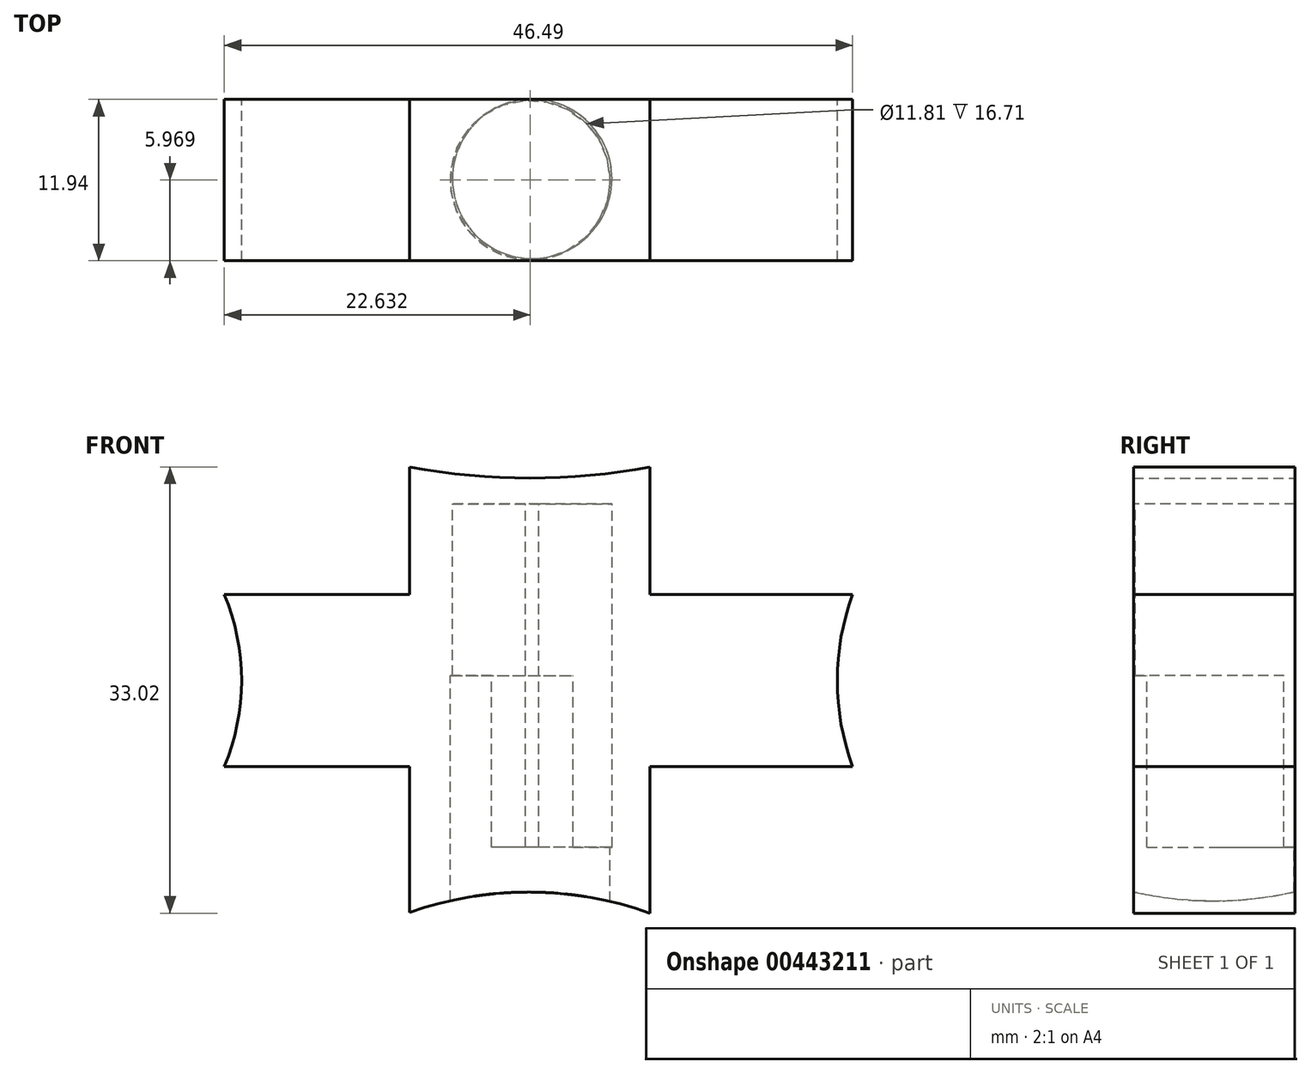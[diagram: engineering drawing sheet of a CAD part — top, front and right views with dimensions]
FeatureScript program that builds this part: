
annotation { "Feature Type Name" : "Feature", "Feature Type Description" : "" }
export const myFeature = defineFeature(function(context is Context, id is Id, definition is map)
    precondition{}
    {
        {
            var Q0;
            Q0=qCreatedBy(makeId("Front.planeOp"),FACE);
            var sketch = newSketch(context, id + "F0", { "sketchPlane" : qUnion([Q0])});
            skLineSegment(sketch, "E0", {"start": v(-15.3, -17.58) * mm, "end": v(-15.3, 15.44) * mm});
            skLineSegment(sketch, "E1.0", {"start": v(-33.08, -17.52) * mm, "end": v(-33.08, 15.44) * mm});
            skLineSegment(sketch, "E2", {"start": v(-15.3, 6) * mm, "end": v(0, 6) * mm});
            skLineSegment(sketch, "E3", {"start": v(-0.3, 6) * mm, "end": v(0, 6) * mm});
            skLineSegment(sketch, "E4", {"start": v(-0.3, -6.74) * mm, "end": v(-15.3, -6.74) * mm});
            skLineSegment(sketch, "E5", {"start": v(-33.08, 6) * mm, "end": v(-46.8, 6) * mm});
            skLineSegment(sketch, "E6", {"start": v(-46.8, -6.74) * mm, "end": v(-33.08, -6.74) * mm});
            skArc(sketch, "E7", {"start": v(-33.08, 15.44) * mm, "mid": v(-24.19, 14.6) * mm, "end": v(-15.3, 15.44) * mm});
            skArc(sketch, "E8", {"start": v(-15.3, -17.58) * mm, "mid": v(-24.18, -16.02) * mm, "end": v(-33.08, -17.52) * mm});
            skArc(sketch, "E9", {"start": v(-46.8, -6.74) * mm, "mid": v(-45.52, -0.37) * mm, "end": v(-46.8, 6) * mm});
            skArc(sketch, "E10", {"start": v(-0.3, 6) * mm, "mid": v(-1.45, -0.37) * mm, "end": v(-0.3, -6.74) * mm});
            skSolve(sketch);
        }
        {
            var Q0;
            Q0 = qSketchRegion(id + "F0", true);
            extrude(context, id + "F1", {"entities" : qUnion([Q0]), "depth" : 11.94 * mm});
        }
        {
            var Q0;
            Q0=qCreatedBy(makeId("Top.planeOp"),FACE);
            var sketch = newSketch(context, id + "F2", { "sketchPlane" : qUnion([Q0])});
            skCircle(sketch, "E11", {"center": v(-24.17, -5.97) * mm, "radius": 5.9 * mm});
            skSolve(sketch);
        }
        {
            var Q0;
            Q0 = qSketchRegion(id + "F2", true);
            extrude(context, id + "F3", {"entities" : qUnion([Q0]), "operationType" : NewBodyOperationType.REMOVE, "endBound" : BoundingType.THROUGH_ALL, "oppositeDirection" : true, "depth" : 25.4 * mm});
        }
        {
            var Q0;
            Q0=qCreatedBy(makeId("Top.planeOp"),FACE);
            var sketch = newSketch(context, id + "F4", { "sketchPlane" : qUnion([Q0])});
            skCircle(sketch, "E12", {"center": v(-24.02, -5.88) * mm, "radius": 5.9 * mm});
            skSolve(sketch);
        }
        {
            var Q0;
            Q0 = qSketchRegion(id + "F4", true);
            extrude(context, id + "F5", {"entities" : qUnion([Q0]), "operationType" : NewBodyOperationType.REMOVE, "endBound" : BoundingType.SYMMETRIC, "oppositeDirection" : true, "depth" : 25.4 * mm});
        }
    });
